# Revit family: Remeha_QuintaPro90_6Boilers-AirDirtSeparator-FreeStanding-LOD5
name_source: partatom
category: Mechanical Equipment
revit_build: Autodesk Revit 2016 (Build: 20150714_1515(x64)
units: mm (PartAtom-declared; Revit-internal decimal feet)

## family parameters
Always vertical = Yes
Cut with Voids When Loaded = Yes
OmniClass Number = 23.75.10.11.14
OmniClass Title = Hot Water Heat Generators
Part Type = Normal
Room Calculation Point = No
Round Connector Dimension = Use Diameter
Shared = No
Work Plane-Based = No

## types (2) — shared parameters
Access Clearance Bottom = 0.00 mm
Access Clearance Front = 1000.00 mm
Access Clearance Left = 600.00 mm
Access Clearance Rear = 0.00 mm
Access Clearance Right = 600.00 mm
Access Clearance Top = 400.00 mm
Air Inlet Connection Size = 0.00 mm
Annually = As Per Attached URL O&M Manual
BMS Links = Yes
Building Regulations Seasonal Efficiency = 95.65
Burner Control Type = Modulating
CE Mark = Yes
Colour = RAL 9016
Condensate Drain Size = 32.00 mm
Condensate Drain Type = Plain
Configuration = Cascade boilers
Control Type = '0 - 10V, Open Therm, Volt free enable, Direct boiler weather compensating control systems available from Remeha as optional extra's.
Dirt Separator Visibility = Yes
Drain Connection Size = 15.00 mm
Drain Connection Type = Threaded
Energy Technology List = https://etl.beis.gov.uk
ErP Energy Label = 0
ErP Rated Efficiency at Full Load = 88.2
ErP Rated Efficiency at Part Load = 97.4
ErP Seasonal Efficiency = 0
Expected Life = 15
External Material = Steel
Features = Remeha's Quinta Pro Cascade systems are compact high efficiency wall hung condensing boilers. Lighter and more efficienct, their small size make them ideally suited to modular arrangments
Finish = High PolishGardner 60 Grad 91EH
Flow and Return Connection Size = 100.00 mm
Flow and Return Connection Type = Flanged
Flow and Return Distribution Size = 65.00 mm
Flue Outer Diameter = 150.00 mm
Flue or Air Intake Classification = B23,B23P,B33,C13,C33,C43,C53,C63,C83,C93
Frequency = 50 Hz
Fuel Connection Size = 50.00 mm
Fuel Connection Type = Flanged
Full Load Current = 0 A
Fuse Rating = 6 A
Gas Consumption rate = 54.6
Gross Weight = 1107.00 kg
Heat Exchanger Material = Aluminium
Heater Operation = Condensing
Hydraulic Resistance at 11C temperature differential = 0.00000
Hydraulic Resistance at 20C temperature differential = 0.14000
IK Rating = Not Required
IP Rating = X4D
IfcExportAs = IfcBoilerType
IfcExportType = NOTDEFINED
Insulation Visibility = Yes
Interlocks = Yes
Load Classification = Power
Manufacturer = Remeha
Manufacturer Website = www.remeha.co.uk
Maximum Gas Inlet Pressure = 0.02500 bar
Maximum Oil Inlet Pressure = 0.00000 bar
Maximum Operating Pressure = 4.00000 bar
Maximum Power Consumption = 125 W
Minimum Flow Rate at 11C temperature differential = 0.0 L/s
Minimum Flow Rate at 20C temperature differential = 1.0 L/s
Minimum Gas Inlet Pressure = 0.01700 bar
Minimum Oil Inlet Pressure = 0.00000 bar
Minimum Operating Pressure = 0.80000 bar
Minimum Power Consumption = 4 W
Model = FreeStanding
Mounting = Floor Standing
NOx Emissions = 29
No Of Boilers = 6
Nominal Gas Inlet Pressure = 0.02000 bar
Nominal Oil Inlet Pressure = 0.00000 bar
Operation and Maintenance Manual = https://www.remeha.co.uk
Optional Fuel = Gas - LPG
Overall Height = 1576.00 mm
Overall Length = 555.00 mm
Overall Width = 3749.00 mm
Primary Fuel = Gas - NG
Product Literature = https://www.remeha.co.uk
Product Model Number = KT1128
Product Range = Quinta Pro Cascade Free-Standing 6 X Quinta Pro 90 with air dirt separator
Rated Criteria = 80/60
Rated Output = 505200 W
Reference Standard = 2009/142/EC : 92/42/EEC
Safety Valve Connection Size = 20.00 mm
Safety Valve Connection Type = Threaded
Shape = Rectangular (Vertical)
Shipping Weight = 0.00 kg
Sound Pressure Level = 52
Starting Current = 0 A
Supply Phase = 1
Turndown Ratio = 5.89:1
Type = Space heating
Voltage = 230 V
Water Content = 201.0 L
Water Treatment Required = Yes
zero-valued in all types: Oil Consumption rate

## per-type parameters (varying)
| type | Flue Connection size |
| 100/150 Conventional Flue Connection - 100 Connector | 100.00 mm |
| 100/150 Concentric Flue Connection - 150 Connector | 150.00 mm |

note: source unit labels omitted for Hydraulic Resistance at 11C temperature differential, Hydraulic Resistance at 20C temperature differential — the stored unit's dimension contradicts the parameter name (converter mislabeling)

## geometry (parser evidence)
native form markers: Blend x2, Sweep x25
no freeform markers — native parametric forms only
